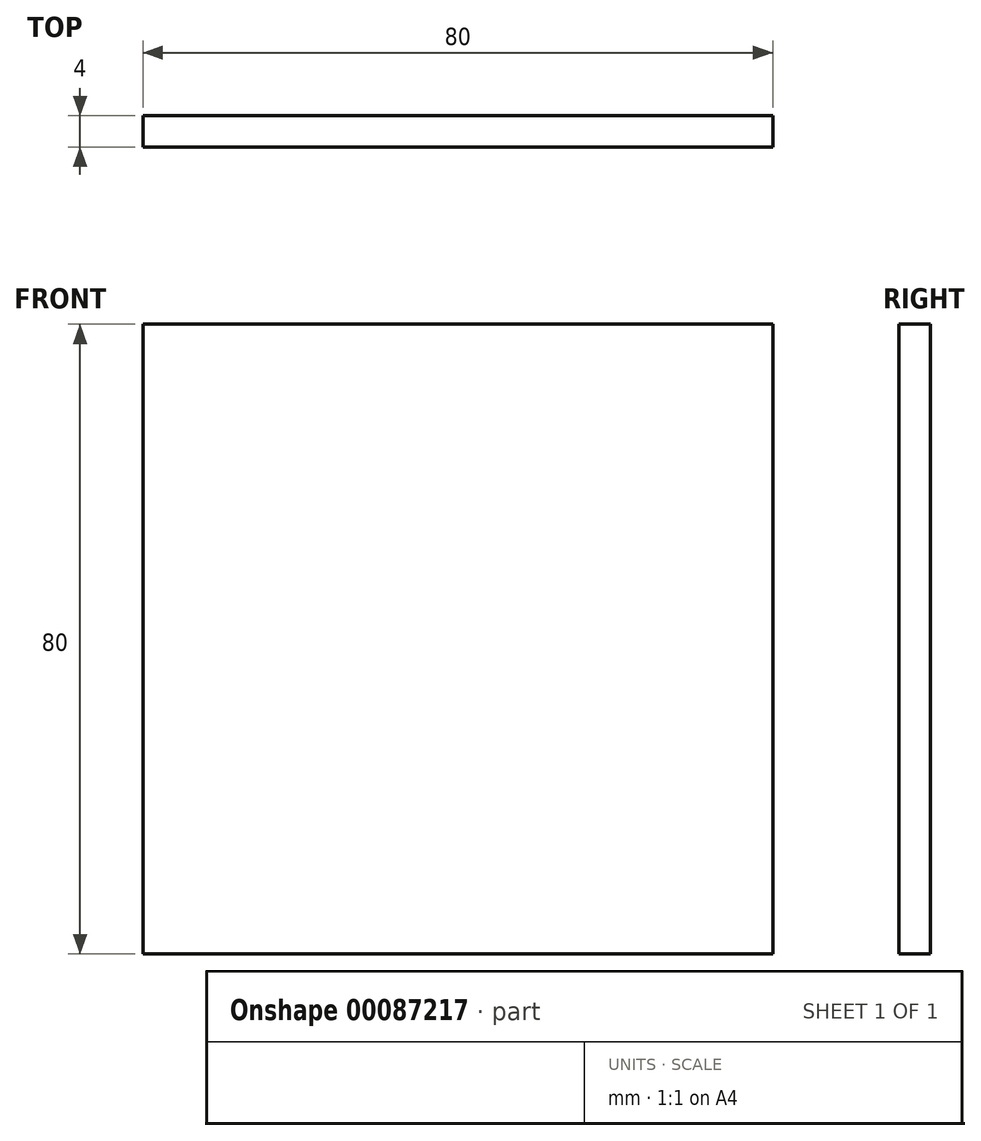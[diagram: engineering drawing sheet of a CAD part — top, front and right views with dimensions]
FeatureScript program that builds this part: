
annotation { "Feature Type Name" : "Feature", "Feature Type Description" : "" }
export const myFeature = defineFeature(function(context is Context, id is Id, definition is map)
    precondition{}
    {
        {
            var Q0;
            Q0=qCreatedBy(makeId("Front.planeOp"),FACE);
            var sketch = newSketch(context, id + "F0", { "sketchPlane" : qUnion([Q0])});
            skLineSegment(sketch, "E0.bottom", {"start": v(35.15, 36.87) * mm, "end": v(-44.85, 36.87) * mm});
            skLineSegment(sketch, "E0.top", {"start": v(35.15, -43.13) * mm, "end": v(-44.85, -43.13) * mm});
            skLineSegment(sketch, "E0.left", {"start": v(35.15, 36.87) * mm, "end": v(35.15, -43.13) * mm});
            skLineSegment(sketch, "E0.right", {"start": v(-44.85, 36.87) * mm, "end": v(-44.85, -43.13) * mm});
            skSolve(sketch);
        }
        {
            var Q0;
            Q0 = qSketchRegion(id + "F0", true);
            extrude(context, id + "F1", {"entities" : qUnion([Q0]), "depth" : 4 * mm});
        }
    });
